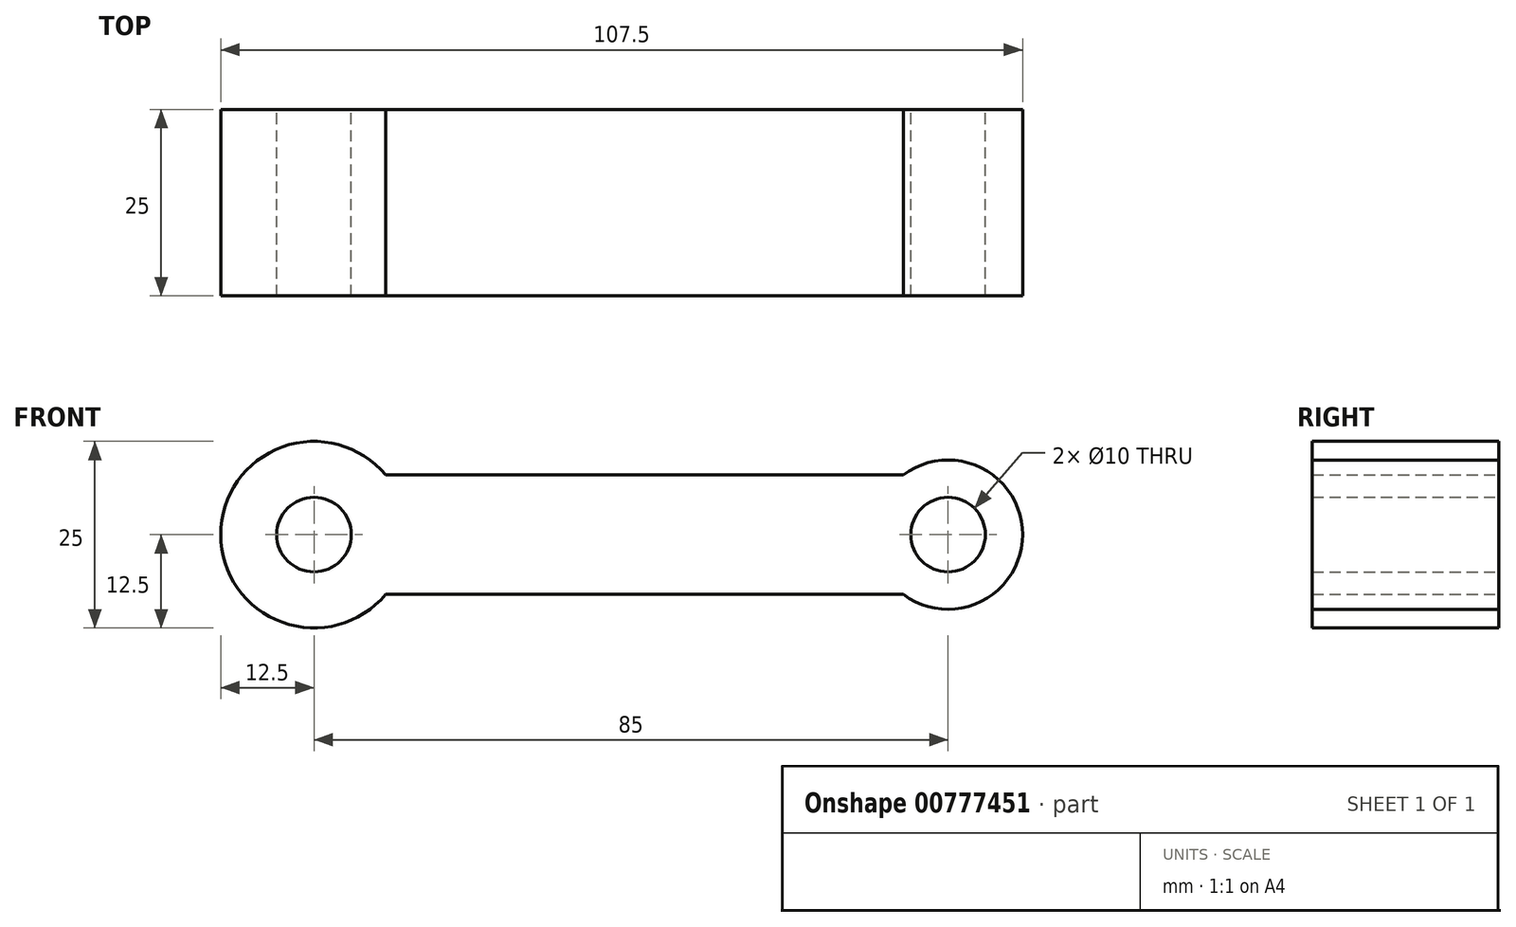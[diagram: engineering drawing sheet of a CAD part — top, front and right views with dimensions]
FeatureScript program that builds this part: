
annotation { "Feature Type Name" : "Feature", "Feature Type Description" : "" }
export const myFeature = defineFeature(function(context is Context, id is Id, definition is map)
    precondition{}
    {
        {
            var Q0;
            Q0=qCreatedBy(makeId("Front.planeOp"),FACE);
            var sketch = newSketch(context, id + "F0", { "sketchPlane" : qUnion([Q0])});
            skCircle(sketch, "E0", {"center": v(0, 0) * mm, "radius": 12.5 * mm});
            skCircle(sketch, "E1", {"center": v(85, 0) * mm, "radius": 10 * mm});
            skLineSegment(sketch, "E2", {"start": v(9.6, 8) * mm, "end": v(79, 8) * mm});
            skLineSegment(sketch, "E3", {"start": v(0, 0) * mm, "end": v(85, 0) * mm, "construction": true});
            skLineSegment(sketch, "E4.MirrorCS", {"start": v(9.6, -8) * mm, "end": v(79, -8) * mm});
            skCircle(sketch, "E5", {"center": v(0, 0) * mm, "radius": 5 * mm});
            skCircle(sketch, "E6", {"center": v(85, 0) * mm, "radius": 5 * mm});
            skSolve(sketch);
        }
        {
            var Q0;
            Q0 = qSketchRegion(id + "F0", true);
            extrude(context, id + "F1", {"entities" : qUnion([Q0]), "depth" : 25 * mm, "offsetDistance" : 25 * mm});
        }
    });
